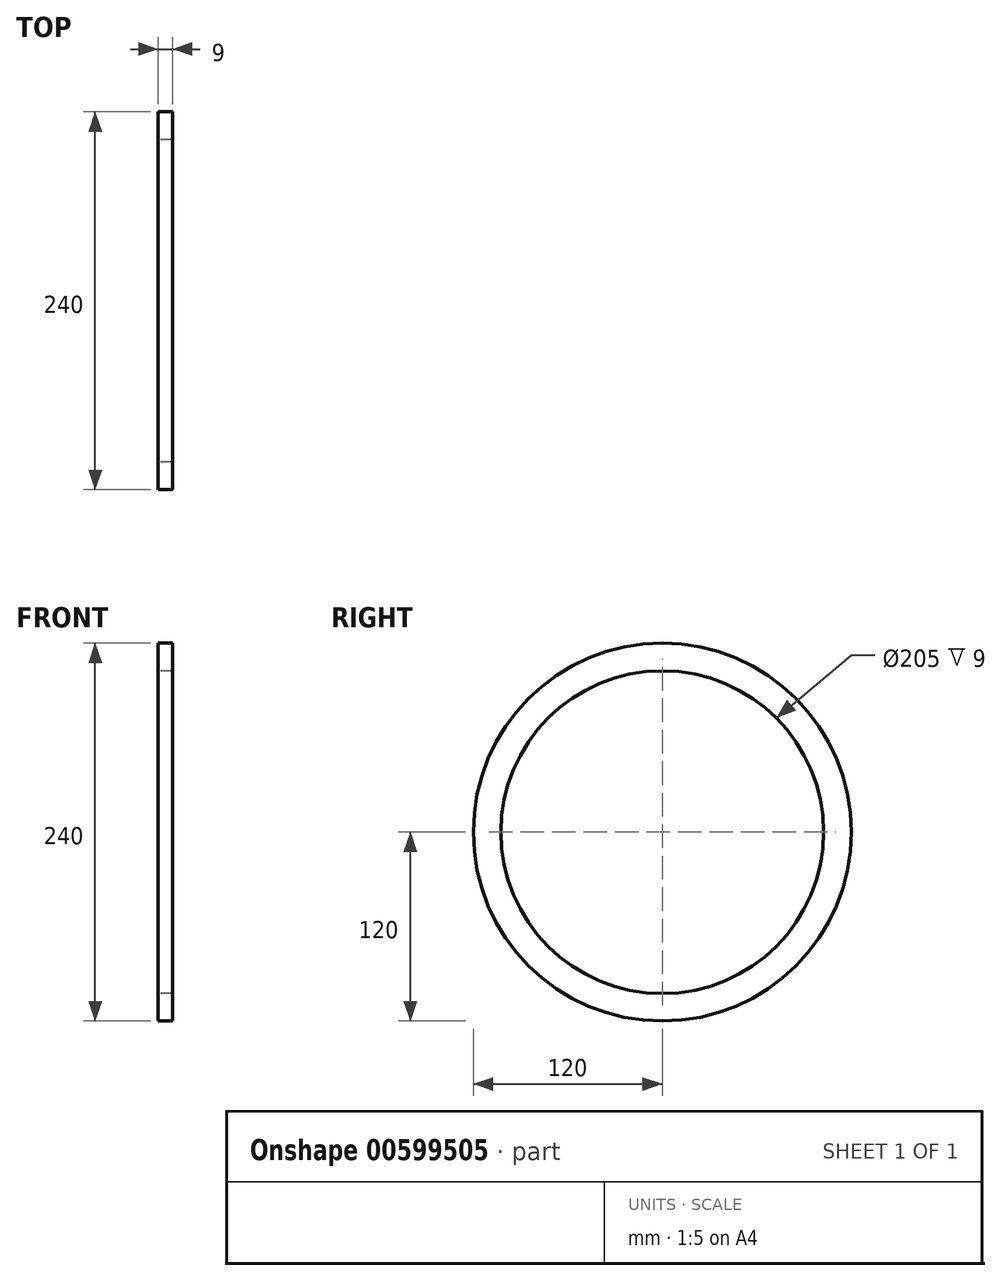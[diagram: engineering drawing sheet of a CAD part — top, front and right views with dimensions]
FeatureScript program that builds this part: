
annotation { "Feature Type Name" : "Feature", "Feature Type Description" : "" }
export const myFeature = defineFeature(function(context is Context, id is Id, definition is map)
    precondition{}
    {
        {
            var Q0;
            Q0=qCreatedBy(makeId("Front.planeOp"),FACE);
            var sketch = newSketch(context, id + "F0", { "sketchPlane" : qUnion([Q0])});
            skLineSegment(sketch, "E0", {"start": v(0, 111.25) * mm, "end": v(0, 0) * mm, "construction": true});
            skLineSegment(sketch, "E1", {"start": v(0, 0) * mm, "end": v(26.93, 0) * mm, "construction": true});
            skLineSegment(sketch, "E2.bottom", {"start": v(-4.5, 120) * mm, "end": v(4.5, 120) * mm});
            skLineSegment(sketch, "E2.top", {"start": v(-4.5, 102.5) * mm, "end": v(4.5, 102.5) * mm});
            skLineSegment(sketch, "E2.left", {"start": v(-4.5, 120) * mm, "end": v(-4.5, 102.5) * mm});
            skLineSegment(sketch, "E2.right", {"start": v(4.5, 120) * mm, "end": v(4.5, 102.5) * mm});
            skPoint(sketch, "E2.middle", {"position": v(0, 111.25) * mm});
            skSolve(sketch);
        }
        {
            var Q0;
            Q0=makeQuery(id+"F0.imprint","IMPRINT",FACE,{"disambiguationData":[TD([[makeQuery(id+"F0.imprint","IMPRINT",EDGE,{"derivedFrom":sQuery(id+"F0.wireOp",EDGE,"E2.bottom")}),-1.0]])]});
            var Q1;
            Q1=sQuery(id+"F0.wireOp",EDGE,"E1");
            revolve(context, id + "F1", {"entities" : qUnion([Q0]), "axis" : qUnion([Q1]), "revolveType" : RevolveType.FULL});
        }
    });
